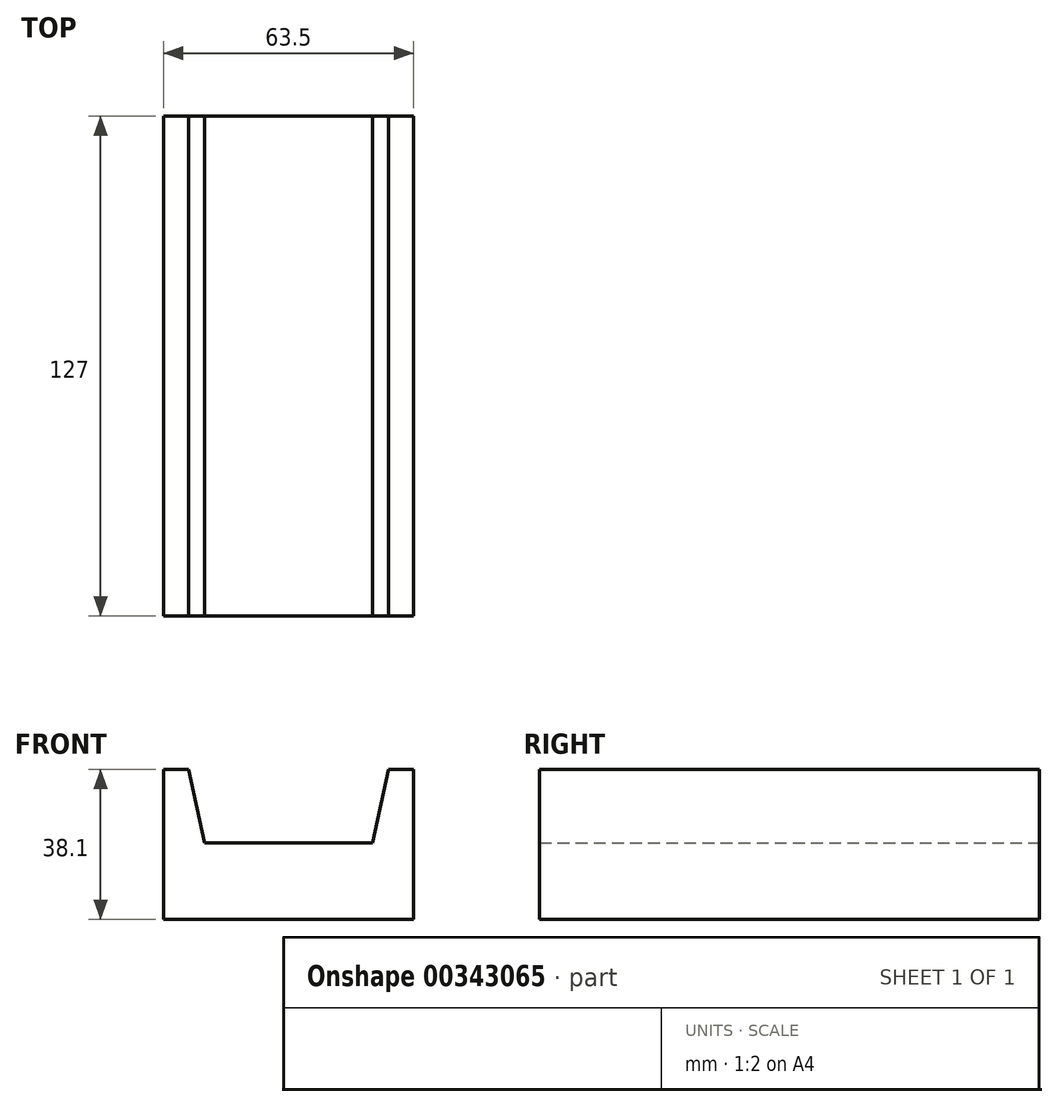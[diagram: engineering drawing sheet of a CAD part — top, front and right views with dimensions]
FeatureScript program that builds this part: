
annotation { "Feature Type Name" : "Feature", "Feature Type Description" : "" }
export const myFeature = defineFeature(function(context is Context, id is Id, definition is map)
    precondition{}
    {
        {
            var Q0;
            Q0=qCreatedBy(makeId("Front.planeOp"),FACE);
            var sketch = newSketch(context, id + "F0", { "sketchPlane" : qUnion([Q0])});
            skLineSegment(sketch, "E0", {"start": v(-57.15, -38.1) * mm, "end": v(6.35, -38.1) * mm});
            skLineSegment(sketch, "E1", {"start": v(6.35, -38.1) * mm, "end": v(6.35, 0) * mm});
            skLineSegment(sketch, "E2", {"start": v(-57.15, -38.1) * mm, "end": v(-57.15, 0) * mm});
            skLineSegment(sketch, "E3", {"start": v(-57.15, 0) * mm, "end": v(-50.8, 0) * mm});
            skLineSegment(sketch, "E4", {"start": v(-50.8, 0) * mm, "end": v(-46.76, -18.62) * mm});
            skLineSegment(sketch, "E5", {"start": v(6.35, 0) * mm, "end": v(0, 0) * mm});
            skLineSegment(sketch, "E6", {"start": v(0, 0) * mm, "end": v(-4.04, -18.62) * mm});
            skLineSegment(sketch, "E7", {"start": v(-4.04, -18.62) * mm, "end": v(-46.76, -18.62) * mm});
            skSolve(sketch);
        }
        {
            var Q0;
            Q0 = qSketchRegion(id + "F0", true);
            extrude(context, id + "F1", {"entities" : qUnion([Q0]), "depth" : 127 * mm});
        }
    });
